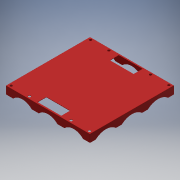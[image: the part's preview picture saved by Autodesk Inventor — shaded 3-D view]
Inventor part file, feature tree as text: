
AUTODESK INVENTOR PART (.ipt)
format: ipt  version: 2018 (Build 220112000, 112)  size: 274,944 bytes
history: native  units: in
note: dims shown in document units (in); Inventor stores cm internally (conversion verified against a paired STEP export)
features: extrude x4, sketch x4, shell x1, fillet x1, projected_geometry x1
ambient origin geometry x8: Origin, YZ Plane, XZ Plane, XY Plane, X Axis, Y Axis, Z Axis, Center Point
bodies: Solid1 (feature_tree)
feature tree (11):
  extrude  "Extrusion1"  Depth=84.75in
  shell  "Shell1"  Thickness=84.75in
  extrude  "Extrusion2"  Depth=13.0in
  extrude  "Extrusion3"  Depth=15.0in
  extrude  "Extrusion4"  Depth=0.25in
  fillet  "Fillet1"  Radius=2.0in
  sketch  "Sketch1"  dims[d0=8.0in d1=84.75in d2=84.75in d3=0.0in]
  sketch  "Sketch2"  dims[d4=0.375in d5=13.0in]
  projected_geometry  "Projected Loop1"
  sketch  "Sketch3"  dims[d6=120.0in d7=0.0in d8=15.0in]
  sketch  "Sketch4"  dims[d9=120.0in d10=0.0in d11=2.5in d14=2.0in d15=2.5in d16=2.5in d17=21.0in d18=2.0in d19=0.7874in d21=80.0in d22=0.7874in d24=79.0in d27=0.7874in d29=80.0in d30=0.7874in d32=42.0in d35=120.0in d36=0.0in d37=24.0in d38=82.0in d39=9.0in d40=9.0in d41=0.25in]
